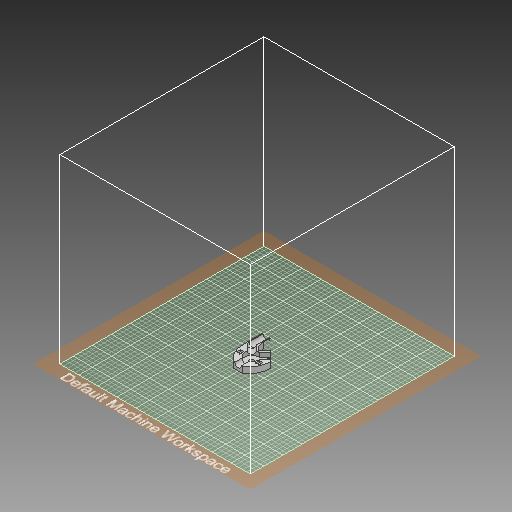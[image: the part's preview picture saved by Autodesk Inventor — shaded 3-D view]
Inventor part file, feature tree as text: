
AUTODESK INVENTOR PART (.ipt)
format: ipt  version: 2019 (Build 230136000, 136)  size: 571,904 bytes
history: native  units: mm
features: sketch x20, extrude x16, projected_geometry x3, sweep x2, other x2, fillet x1
ambient origin geometry x8: Origin, YZ Plane, XZ Plane, XY Plane, X Axis, Y Axis, Z Axis, Center Point
bodies: Body1 (feature_tree)
feature tree (44):
  extrude  "Extrusion2"  Depth=80.0mm
  sketch  "Esquisse3"
  sweep  "Balayage1"
  extrude  "Extrusion6"  Depth=32.0mm
  extrude  "Extrusion7"  Depth=18.0mm TaperAngle=0.0deg
  extrude  "Extrusion8"  TaperAngle=135.0deg  [1 undecoded]
  sketch  "Esquisse11"
  sketch  "Esquisse12"
  other  "Plan de construction1"
  sketch  "Esquisse13"
  extrude  "Extrusion9"  Depth=23.0mm
  extrude  "Extrusion10"  Depth=14.0mm
  other  "Plan de construction2"
  sketch  "Esquisse14"
  extrude  "Extrusion11"  Depth=4.0mm
  extrude  "Extrusion12"  TaperAngle=0.0deg  [1 undecoded]
  extrude  "Extrusion13"  Depth=4.0mm TaperAngle=0.0deg
  extrude  "Extrusion14"  Depth=10.0mm
  extrude  "Extrusion15"  Depth=4.0mm TaperAngle=0.0deg
  sketch  "Esquisse20"
  sketch  "Esquisse21"
  sketch  "Esquisse24"
  extrude  "Extrusion17"  Depth=2.0mm
  sweep  "Balayage4"
  extrude  "Extrusion18"  Depth=35.0mm
  extrude  "Extrusion19"  Depth=17.5mm
  extrude  "Extrusion20"  Depth=8.5mm
  extrude  "Extrusion21"  Depth=12.0mm TaperAngle=0.0deg
  fillet  "Congé1"  Radius=30.0mm
  sketch  "Esquisse2"
  sketch  "Esquisse4"
  sketch  "Esquisse8"
  sketch  "Esquisse9"
  sketch  "Esquisse10"
  sketch  "Esquisse16"
  projected_geometry  "Boucle projetée3"
  sketch  "Esquisse18"
  sketch  "Esquisse19"
  projected_geometry  "Boucle projetée4"
  projected_geometry  "Boucle projetée6"
  sketch  "Esquisse25"
  sketch  "Esquisse26"
  sketch  "Esquisse27"
  sketch  "Esquisse28"
note: 2 required parameter values undecoded (feature->parameter linkage not recoverable at this tier; creation-order binding heuristic only, values carry confidence <= 0.55)
